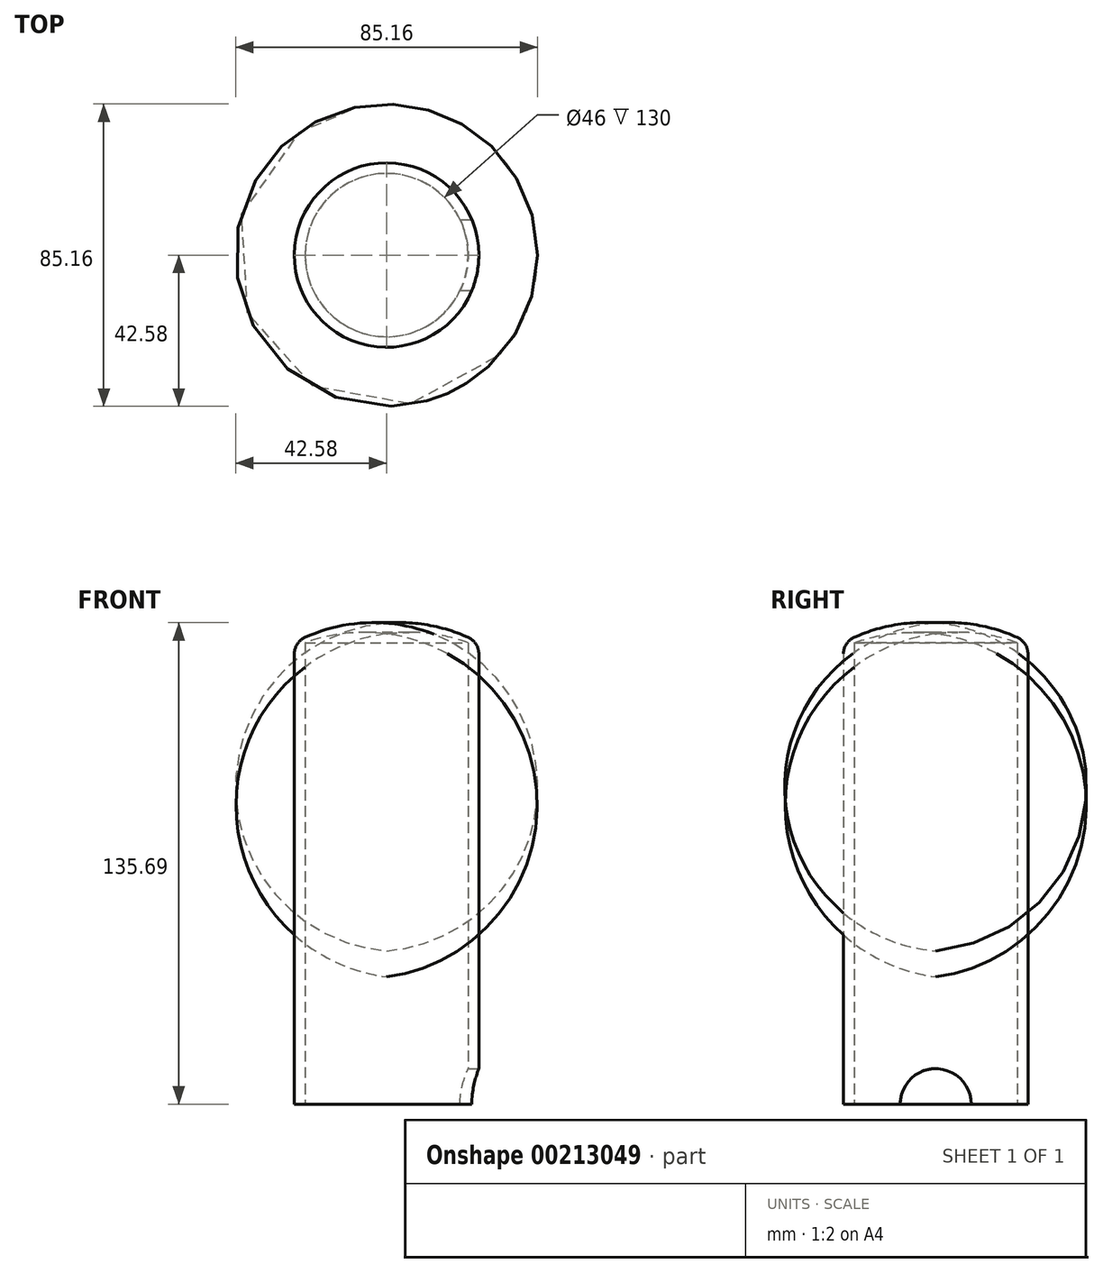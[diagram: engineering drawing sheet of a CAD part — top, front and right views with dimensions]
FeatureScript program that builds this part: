
annotation { "Feature Type Name" : "Feature", "Feature Type Description" : "" }
export const myFeature = defineFeature(function(context is Context, id is Id, definition is map)
    precondition{}
    {
        {
            var Q0;
            Q0=qCreatedBy(makeId("Front.planeOp"),FACE);
            var sketch = newSketch(context, id + "F0", { "sketchPlane" : qUnion([Q0])});
            skLineSegment(sketch, "E0", {"start": v(0, 0) * mm, "end": v(-23, 0) * mm});
            skLineSegment(sketch, "E1", {"start": v(-23, 0) * mm, "end": v(-23, 130) * mm});
            skLineSegment(sketch, "E2", {"start": v(-26, 0) * mm, "end": v(-26, 130) * mm});
            skLineSegment(sketch, "E3", {"start": v(-23, 0) * mm, "end": v(-26, 0) * mm});
            skArc(sketch, "E4", {"start": v(0, 135.54) * mm, "mid": v(-13.4, 134.67) * mm, "end": v(-26, 130) * mm});
            skArc(sketch, "E5", {"start": v(0, 132.54) * mm, "mid": v(-11.65, 132.65) * mm, "end": v(-23, 130) * mm});
            skLineSegment(sketch, "E6", {"start": v(0, 135.54) * mm, "end": v(0, 132.54) * mm});
            skLineSegment(sketch, "E7", {"start": v(0, 0) * mm, "end": v(0, 16.82) * mm});
            skSolve(sketch);
        }
        {
            var Q0;
            Q0=makeQuery(id+"F0.imprint","IMPRINT",FACE,{"disambiguationData":[TD([[makeQuery(id+"F0.imprint","IMPRINT",EDGE,{"derivedFrom":sQuery(id+"F0.wireOp",EDGE,"E1")}),1.0]])]});
            var Q1;
            Q1=sQuery(id+"F0.wireOp",EDGE,"E7");
            revolve(context, id + "F1", {"entities" : qUnion([Q0]), "axis" : qUnion([Q1]), "revolveType" : RevolveType.FULL});
        }
        {
            var Q0;
            Q0=makeQuery(id+"F1.opRevolve","SWEPT_EDGE",EDGE,{"disambiguationData":[OSD([sQuery(id+"F0.wireOp",EDGE,"E2"),sQuery(id+"F0.wireOp",EDGE,"E4")])]});
            fillet(context, id + "F2", {"entities" : qUnion([Q0]), "radius" : 5 * mm, "tangentPropagation" : true, "allowEdgeOverflow" : false});
        }
        {
            var Q0;
            Q0=qCreatedBy(makeId("Right.planeOp"),FACE);
            cPlane(context, id + "F3", {"entities" : qUnion([Q0]), "cplaneType" : CPlaneType.OFFSET, "offset" : 40 * mm, "width" : 150 * mm, "height" : 150 * mm});
        }
        {
            var Q0;
            Q0=qCreatedBy(id+"F3.planeOp",FACE);
            var sketch = newSketch(context, id + "F4", { "sketchPlane" : qUnion([Q0])});
            skCircle(sketch, "E8", {"center": v(0, 0) * mm, "radius": 10 * mm});
            skSolve(sketch);
        }
        {
            var Q0;
            Q0=makeQuery(id+"F4.imprint","IMPRINT",FACE,{"disambiguationData":[TD([[makeQuery(id+"F4.imprint","IMPRINT",EDGE,{"derivedFrom":sQuery(id+"F4.wireOp",EDGE,"E8")}),1.0]])]});
            extrude(context, id + "F5", {"entities" : qUnion([Q0]), "operationType" : NewBodyOperationType.REMOVE, "oppositeDirection" : true, "depth" : 30 * mm});
        }
    });
